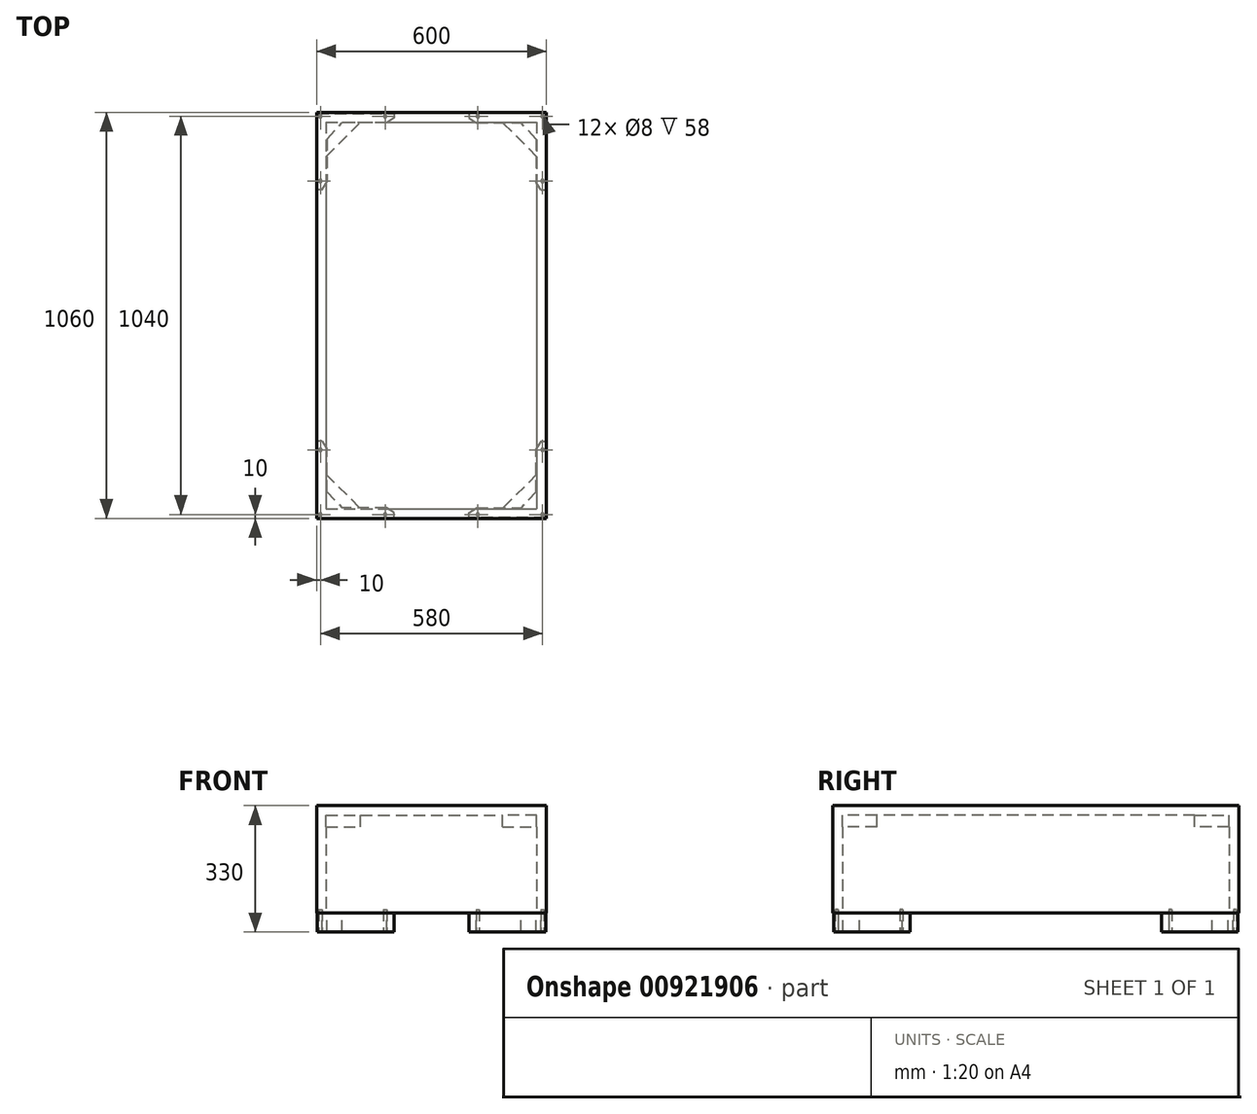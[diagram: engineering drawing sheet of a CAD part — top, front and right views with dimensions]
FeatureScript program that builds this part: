
annotation { "Feature Type Name" : "Feature", "Feature Type Description" : "" }
export const myFeature = defineFeature(function(context is Context, id is Id, definition is map)
    precondition{}
    {
        {
            var Q0;
            Q0=qCreatedBy(makeId("Top.planeOp"),FACE);
            var sketch = newSketch(context, id + "F0", { "sketchPlane" : qUnion([Q0])});
            skLineSegment(sketch, "E0.bottom", {"start": v(0, 0) * mm, "end": v(600, 0) * mm});
            skLineSegment(sketch, "E0.top", {"start": v(0, -1060) * mm, "end": v(600, -1060) * mm});
            skLineSegment(sketch, "E0.left", {"start": v(0, 0) * mm, "end": v(0, -1060) * mm});
            skLineSegment(sketch, "E0.right", {"start": v(600, 0) * mm, "end": v(600, -1060) * mm});
            skSolve(sketch);
        }
        {
            var Q0;
            Q0 = qSketchRegion(id + "F0", true);
            extrude(context, id + "F1", {"entities" : qUnion([Q0]), "depth" : 280 * mm, "offsetDistance" : 25 * mm});
        }
        {
            var Q0;
            Q0=makeQuery(id+"F1.opExtrude","CAP_FACE",FACE,{"disambiguationData":[OSD([sQuery(id+"F0.wireOp",EDGE,"E0.bottom"),sQuery(id+"F0.wireOp",EDGE,"E0.top"),sQuery(id+"F0.wireOp",EDGE,"E0.left"),sQuery(id+"F0.wireOp",EDGE,"E0.right")])],"isStart":true});
            shell(context, id + "F2", {"entities" : qUnion([Q0]), "thickness" : 25 * mm});
        }
        {
            var Q0;
            Q0=makeQuery(id+"F1.opExtrude","CAP_FACE",FACE,{"disambiguationData":[OSD([sQuery(id+"F0.wireOp",EDGE,"E0.bottom"),sQuery(id+"F0.wireOp",EDGE,"E0.top"),sQuery(id+"F0.wireOp",EDGE,"E0.left"),sQuery(id+"F0.wireOp",EDGE,"E0.right")])],"isStart":true});
            var sketch = newSketch(context, id + "F3", { "sketchPlane" : qUnion([Q0])});
            skLineSegment(sketch, "E1", {"start": v(179, 1060) * mm, "end": v(179, 1050) * mm, "construction": true});
            skLineSegment(sketch, "E2", {"start": v(0, 881) * mm, "end": v(10, 881) * mm, "construction": true});
            skLineSegment(sketch, "E3", {"start": v(179, 1050) * mm, "end": v(-86.82, 1050) * mm, "construction": true});
            skLineSegment(sketch, "E4", {"start": v(10, 881) * mm, "end": v(10, 1098.47) * mm, "construction": true});
            skCircle(sketch, "E5", {"center": v(10, 1050) * mm, "radius": 4 * mm});
            skCircle(sketch, "E6", {"center": v(10, 881) * mm, "radius": 4 * mm});
            skCircle(sketch, "E7", {"center": v(179, 1050) * mm, "radius": 4 * mm});
            skLineSegment(sketch, "E8", {"start": v(300, 1060) * mm, "end": v(300, 0) * mm, "construction": true});
            skLineSegment(sketch, "E9", {"start": v(600, 530) * mm, "end": v(0, 530) * mm, "construction": true});
            skCircle(sketch, "E10.MirrorC", {"center": v(590, 1050) * mm, "radius": 4 * mm});
            skCircle(sketch, "E11.MirrorC", {"center": v(421, 1050) * mm, "radius": 4 * mm});
            skCircle(sketch, "E12.MirrorC", {"center": v(590, 881) * mm, "radius": 4 * mm});
            skCircle(sketch, "E13.MirrorC", {"center": v(10, 179) * mm, "radius": 4 * mm});
            skCircle(sketch, "E14.MirrorC", {"center": v(10, 10) * mm, "radius": 4 * mm});
            skCircle(sketch, "E15.MirrorC", {"center": v(179, 10) * mm, "radius": 4 * mm});
            skCircle(sketch, "E16.MirrorC", {"center": v(421, 10) * mm, "radius": 4 * mm});
            skCircle(sketch, "E17.MirrorC", {"center": v(590, 10) * mm, "radius": 4 * mm});
            skCircle(sketch, "E18.MirrorC", {"center": v(590, 179) * mm, "radius": 4 * mm});
            skSolve(sketch);
        }
        {
            var Q0;
            Q0 = qSketchRegion(id + "F3", true);
            extrude(context, id + "F4", {"entities" : qUnion([Q0]), "operationType" : NewBodyOperationType.REMOVE, "oppositeDirection" : true, "depth" : 8 * mm, "offsetDistance" : 25 * mm});
        }
        {
            var Q0;
            Q0=makeQuery(id+"F2.opShell","OFFSET_FACE",FACE,{"disambiguationData":[OSD([sQuery(id+"F0.wireOp",EDGE,"E0.bottom"),sQuery(id+"F0.wireOp",EDGE,"E0.top"),sQuery(id+"F0.wireOp",EDGE,"E0.left"),sQuery(id+"F0.wireOp",EDGE,"E0.right")])]});
            var sketch = newSketch(context, id + "F5", { "sketchPlane" : qUnion([Q0])});
            skLineSegment(sketch, "E19", {"start": v(25, 1035) * mm, "end": v(25, 945) * mm});
            skLineSegment(sketch, "E20", {"start": v(25, 945) * mm, "end": v(115, 1035) * mm});
            skLineSegment(sketch, "E21", {"start": v(115, 1035) * mm, "end": v(25, 1035) * mm});
            skLineSegment(sketch, "E22", {"start": v(300, 1035) * mm, "end": v(300, 25) * mm});
            skLineSegment(sketch, "E23", {"start": v(25, 530) * mm, "end": v(575, 530) * mm});
            skLineSegment(sketch, "E24.MirrorCS", {"start": v(575, 945) * mm, "end": v(485, 1035) * mm});
            skLineSegment(sketch, "E25.MirrorCS", {"start": v(485, 1035) * mm, "end": v(575, 1035) * mm});
            skLineSegment(sketch, "E26.MirrorCS", {"start": v(575, 1035) * mm, "end": v(575, 945) * mm});
            skLineSegment(sketch, "E27.MirrorCS", {"start": v(25, 115) * mm, "end": v(115, 25) * mm});
            skLineSegment(sketch, "E28.MirrorCS", {"start": v(115, 25) * mm, "end": v(25, 25) * mm});
            skLineSegment(sketch, "E29.MirrorCS", {"start": v(25, 25) * mm, "end": v(25, 115) * mm});
            skLineSegment(sketch, "E30.MirrorCS", {"start": v(575, 115) * mm, "end": v(485, 25) * mm});
            skLineSegment(sketch, "E31.MirrorCS", {"start": v(485, 25) * mm, "end": v(575, 25) * mm});
            skLineSegment(sketch, "E32.MirrorCS", {"start": v(575, 25) * mm, "end": v(575, 115) * mm});
            skSolve(sketch);
        }
        {
            var Q0;
            Q0 = qSketchRegion(id + "F5", true);
            extrude(context, id + "F6", {"entities" : qUnion([Q0]), "operationType" : NewBodyOperationType.ADD, "depth" : 30 * mm, "offsetDistance" : 25 * mm});
        }
        {
            var Q0;
            Q0=makeQuery(id+"F1.opExtrude","CAP_FACE",FACE,{"disambiguationData":[OSD([sQuery(id+"F0.wireOp",EDGE,"E0.bottom"),sQuery(id+"F0.wireOp",EDGE,"E0.top"),sQuery(id+"F0.wireOp",EDGE,"E0.left"),sQuery(id+"F0.wireOp",EDGE,"E0.right")])],"isStart":true});
            var sketch = newSketch(context, id + "F7", { "sketchPlane" : qUnion([Q0])});
            skLineSegment(sketch, "E33", {"start": v(0, 955) * mm, "end": v(30, 955) * mm, "construction": true});
            skLineSegment(sketch, "E34", {"start": v(105, 1060) * mm, "end": v(105, 1030) * mm, "construction": true});
            skLineSegment(sketch, "E35", {"start": v(30, 1060) * mm, "end": v(30, 815.36) * mm, "construction": true});
            skLineSegment(sketch, "E36", {"start": v(105, 1030) * mm, "end": v(0, 1030) * mm});
            skLineSegment(sketch, "E37", {"start": v(0, 1030) * mm, "end": v(337.53, 1030) * mm, "construction": true});
            skLineSegment(sketch, "E38", {"start": v(0, 1060) * mm, "end": v(30, 1030) * mm});
            skSolve(sketch);
        }
        {
            var Q0;
            {var subQ2=sQuery(id+"F0.wireOp",EDGE,"E0.bottom");var subQ3=makeQuery(id+"F1.opExtrude","CAP_EDGE",EDGE,{"disambiguationData":[OSD([subQ2])],"isStart":true});Q0=makeQuery(id+"F7.imprint","IMPRINT",FACE,{"disambiguationData":[TD([[makeQuery(id+"F7.imprint","IMPRINT",EDGE,{"derivedFrom":subQ3}),1.0]])]});}
            var sketch = newSketch(context, id + "F8", { "sketchPlane" : qUnion([Q0])});
            skLineSegment(sketch, "E39", {"start": v(2, 1058) * mm, "end": v(202, 1058) * mm});
            skLineSegment(sketch, "E40", {"start": v(202, 1058) * mm, "end": v(202, 1045.5) * mm});
            skLineSegment(sketch, "E41", {"start": v(182.78, 1033) * mm, "end": v(66.77, 1033) * mm});
            skLineSegment(sketch, "E42", {"start": v(27, 990.7) * mm, "end": v(27, 878.24) * mm});
            skLineSegment(sketch, "E43", {"start": v(14.5, 858) * mm, "end": v(2, 858) * mm});
            skLineSegment(sketch, "E44", {"start": v(2, 858) * mm, "end": v(2, 1058) * mm});
            skLineSegment(sketch, "E45", {"start": v(14.5, 858) * mm, "end": v(27, 878.24) * mm});
            skLineSegment(sketch, "E46", {"start": v(202, 1045.5) * mm, "end": v(182.78, 1033) * mm});
            skPoint(sketch, "E47.orphan", {"position": v(202, 1033) * mm});
            skPoint(sketch, "E48.orphan", {"position": v(27, 858) * mm});
            skLineSegment(sketch, "E49", {"start": v(27, 990.7) * mm, "end": v(66.77, 1033) * mm});
            skLineSegment(sketch, "E50", {"start": v(0, 1060) * mm, "end": v(600, 1060) * mm, "construction": true});
            skLineSegment(sketch, "E51", {"start": v(2, 1018.14) * mm, "end": v(0, 1018.14) * mm});
            skLineSegment(sketch, "E52", {"start": v(300, 1060) * mm, "end": v(300, 0) * mm, "construction": true});
            skLineSegment(sketch, "E53", {"start": v(0, 1060) * mm, "end": v(0, 0) * mm, "construction": true});
            skLineSegment(sketch, "E54", {"start": v(0, 530) * mm, "end": v(634.75, 530) * mm, "construction": true});
            skLineSegment(sketch, "E55.MirrorCS", {"start": v(300, 0) * mm, "end": v(300, 1060) * mm, "construction": true});
            skLineSegment(sketch, "E56.MirrorCS", {"start": v(573, 990.7) * mm, "end": v(533.23, 1033) * mm});
            skLineSegment(sketch, "E57.MirrorCS", {"start": v(573, 990.7) * mm, "end": v(573, 878.24) * mm});
            skLineSegment(sketch, "E58.MirrorCS", {"start": v(585.5, 858) * mm, "end": v(573, 878.24) * mm});
            skLineSegment(sketch, "E59.MirrorCS", {"start": v(585.5, 858) * mm, "end": v(598, 858) * mm});
            skLineSegment(sketch, "E60.MirrorCS", {"start": v(598, 858) * mm, "end": v(598, 1058) * mm});
            skLineSegment(sketch, "E61.MirrorCS", {"start": v(598, 1058) * mm, "end": v(398, 1058) * mm});
            skLineSegment(sketch, "E62.MirrorCS", {"start": v(398, 1058) * mm, "end": v(398, 1045.5) * mm});
            skLineSegment(sketch, "E63.MirrorCS", {"start": v(398, 1045.5) * mm, "end": v(417.22, 1033) * mm});
            skLineSegment(sketch, "E64.MirrorCS", {"start": v(417.22, 1033) * mm, "end": v(533.23, 1033) * mm});
            skLineSegment(sketch, "E65.MirrorCS", {"start": v(2, 202) * mm, "end": v(2, 2) * mm});
            skLineSegment(sketch, "E66.MirrorCS", {"start": v(14.5, 202) * mm, "end": v(2, 202) * mm});
            skLineSegment(sketch, "E67.MirrorCS", {"start": v(27, 69.3) * mm, "end": v(27, 181.76) * mm});
            skLineSegment(sketch, "E68.MirrorCS", {"start": v(27, 69.3) * mm, "end": v(66.77, 27) * mm});
            skLineSegment(sketch, "E69.MirrorCS", {"start": v(2, 2) * mm, "end": v(202, 2) * mm});
            skLineSegment(sketch, "E70.MirrorCS", {"start": v(182.78, 27) * mm, "end": v(66.77, 27) * mm});
            skLineSegment(sketch, "E71.MirrorCS", {"start": v(202, 14.5) * mm, "end": v(182.78, 27) * mm});
            skLineSegment(sketch, "E72.MirrorCS", {"start": v(202, 2) * mm, "end": v(202, 14.5) * mm});
            skLineSegment(sketch, "E73.MirrorCS", {"start": v(14.5, 202) * mm, "end": v(27, 181.76) * mm});
            skLineSegment(sketch, "E74.MirrorCS", {"start": v(417.22, 27) * mm, "end": v(533.23, 27) * mm});
            skLineSegment(sketch, "E75.MirrorCS", {"start": v(398, 14.5) * mm, "end": v(417.22, 27) * mm});
            skLineSegment(sketch, "E76.MirrorCS", {"start": v(398, 2) * mm, "end": v(398, 14.5) * mm});
            skLineSegment(sketch, "E77.MirrorCS", {"start": v(598, 2) * mm, "end": v(398, 2) * mm});
            skLineSegment(sketch, "E78.MirrorCS", {"start": v(598, 202) * mm, "end": v(598, 2) * mm});
            skLineSegment(sketch, "E79.MirrorCS", {"start": v(585.5, 202) * mm, "end": v(598, 202) * mm});
            skLineSegment(sketch, "E80.MirrorCS", {"start": v(585.5, 202) * mm, "end": v(573, 181.76) * mm});
            skLineSegment(sketch, "E81.MirrorCS", {"start": v(573, 69.3) * mm, "end": v(533.23, 27) * mm});
            skLineSegment(sketch, "E82.MirrorCS", {"start": v(573, 69.3) * mm, "end": v(573, 181.76) * mm});
            skSolve(sketch);
        }
        {
            var Q0;
            Q0 = qSketchRegion(id + "F8", true);
            extrude(context, id + "F9", {"entities" : qUnion([Q0]), "operationType" : NewBodyOperationType.ADD, "depth" : 50 * mm, "offsetDistance" : 25 * mm});
        }
        {
            var Q0;
            Q0 = qSketchRegion(id + "F8", true);
            extrude(context, id + "F10", {"entities" : qUnion([Q0]), "operationType" : NewBodyOperationType.ADD, "depth" : 50 * mm, "offsetDistance" : 25 * mm});
        }
        {
            var Q0;
            Q0 = qSketchRegion(id + "F3", true);
            extrude(context, id + "F11", {"entities" : qUnion([Q0]), "operationType" : NewBodyOperationType.REMOVE, "endBound" : BoundingType.THROUGH_ALL, "depth" : 25 * mm, "offsetDistance" : 25 * mm});
        }
    });
